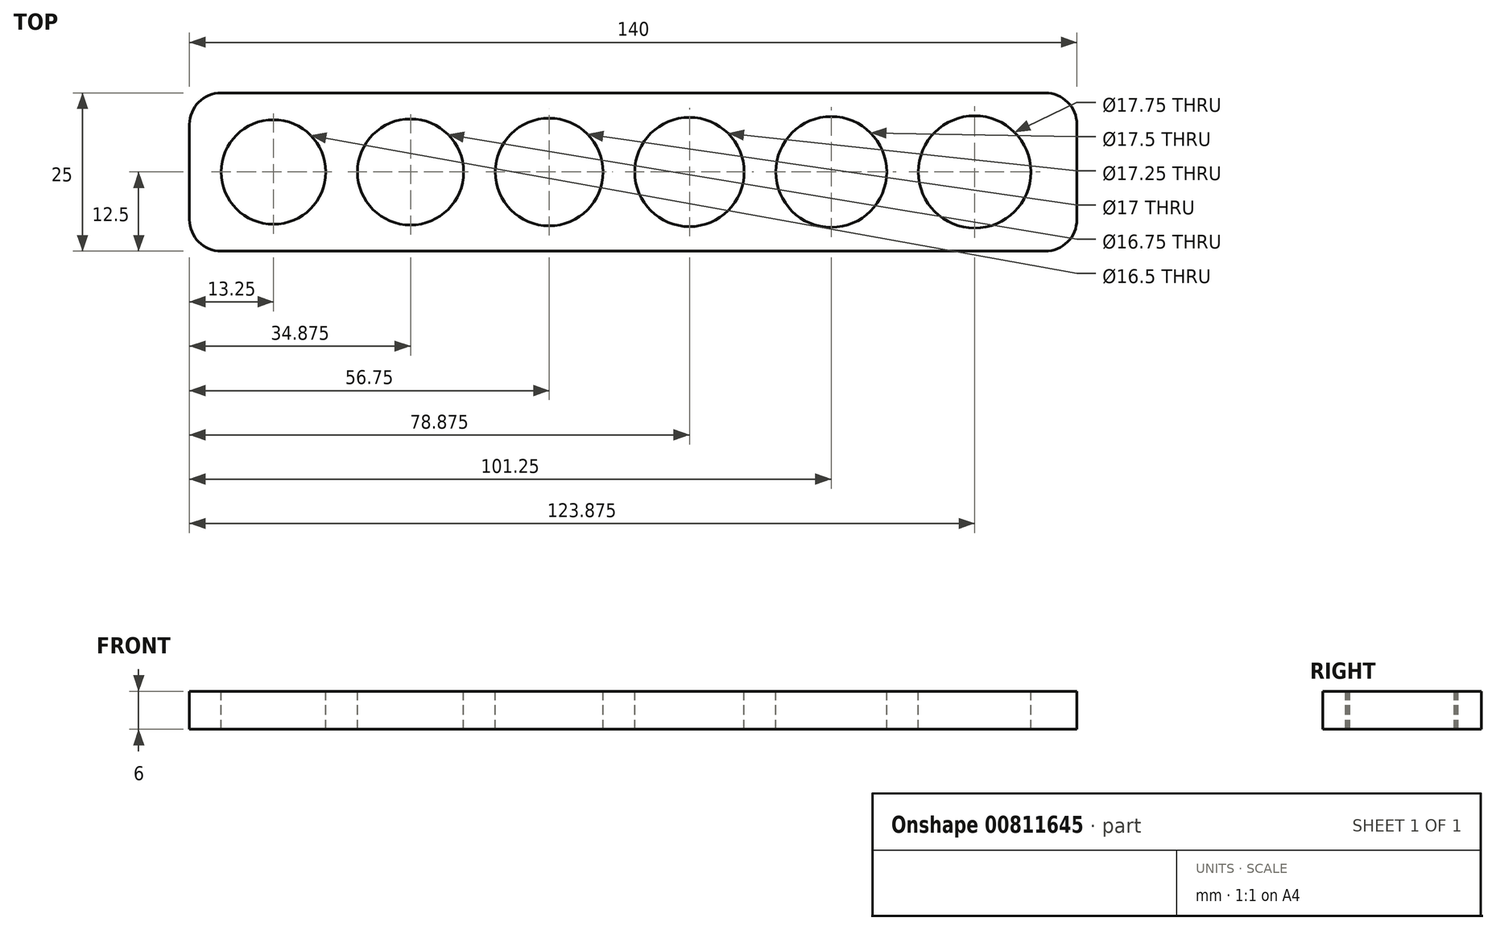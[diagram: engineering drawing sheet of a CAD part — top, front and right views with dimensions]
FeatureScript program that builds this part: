
annotation { "Feature Type Name" : "Feature", "Feature Type Description" : "" }
export const myFeature = defineFeature(function(context is Context, id is Id, definition is map)
    precondition{}
    {
        {
            var Q0;
            Q0=qCreatedBy(makeId("Top.planeOp"),FACE);
            var sketch = newSketch(context, id + "F0", { "sketchPlane" : qUnion([Q0])});
            skLineSegment(sketch, "E0.bottom", {"start": v(-65, 12.5) * mm, "end": v(65, 12.5) * mm});
            skLineSegment(sketch, "E0.top", {"start": v(-65, -12.5) * mm, "end": v(65, -12.5) * mm});
            skLineSegment(sketch, "E0.left", {"start": v(-70, 7.5) * mm, "end": v(-70, -7.5) * mm});
            skLineSegment(sketch, "E0.right", {"start": v(70, 7.5) * mm, "end": v(70, -7.5) * mm});
            skPoint(sketch, "E1.visualSharp", {"position": v(-70, 12.5) * mm});
            skArc(sketch, "E1.filletArc", {"start": v(-65, 12.5) * mm, "mid": v(-68.54, 11.04) * mm, "end": v(-70, 7.5) * mm});
            skPoint(sketch, "E2.visualSharp", {"position": v(70, 12.5) * mm});
            skArc(sketch, "E2.filletArc", {"start": v(70, 7.5) * mm, "mid": v(68.54, 11.04) * mm, "end": v(65, 12.5) * mm});
            skPoint(sketch, "E3.visualSharp", {"position": v(70, -12.5) * mm});
            skArc(sketch, "E3.filletArc", {"start": v(65, -12.5) * mm, "mid": v(68.54, -11.04) * mm, "end": v(70, -7.5) * mm});
            skPoint(sketch, "E4.visualSharp", {"position": v(-70, -12.5) * mm});
            skArc(sketch, "E4.filletArc", {"start": v(-70, -7.5) * mm, "mid": v(-68.54, -11.04) * mm, "end": v(-65, -12.5) * mm});
            skSolve(sketch);
        }
        {
            var Q0;
            Q0=makeQuery(id+"F0.imprint","IMPRINT",FACE,{"disambiguationData":[TD([[makeQuery(id+"F0.imprint","IMPRINT",EDGE,{"derivedFrom":sQuery(id+"F0.wireOp",EDGE,"E0.bottom")}),-1.0]])]});
            extrude(context, id + "F1", {"entities" : qUnion([Q0]), "depth" : 6 * mm, "offsetDistance" : 25 * mm});
        }
        {
            var Q0;
            Q0=makeQuery(id+"F1.opExtrude","CAP_FACE",FACE,{"disambiguationData":[OSD([sQuery(id+"F0.wireOp",EDGE,"E0.bottom"),sQuery(id+"F0.wireOp",EDGE,"E0.top"),sQuery(id+"F0.wireOp",EDGE,"E0.left"),sQuery(id+"F0.wireOp",EDGE,"E0.right")])],"isStart":false});
            var sketch = newSketch(context, id + "F2", { "sketchPlane" : qUnion([Q0])});
            skCircle(sketch, "E5", {"center": v(-56.75, 0) * mm, "radius": 8.25 * mm});
            skCircle(sketch, "E6", {"center": v(-35.12, 0) * mm, "radius": 8.38 * mm});
            skCircle(sketch, "E7", {"center": v(-13.25, 0) * mm, "radius": 8.5 * mm});
            skCircle(sketch, "E8", {"center": v(8.88, 0) * mm, "radius": 8.62 * mm});
            skCircle(sketch, "E9", {"center": v(31.25, 0) * mm, "radius": 8.75 * mm});
            skCircle(sketch, "E10", {"center": v(53.88, 0) * mm, "radius": 8.88 * mm});
            skSolve(sketch);
        }
        {
            var Q0;
            Q0 = qSketchRegion(id + "F2", true);
            extrude(context, id + "F3", {"entities" : qUnion([Q0]), "operationType" : NewBodyOperationType.REMOVE, "endBound" : BoundingType.THROUGH_ALL, "oppositeDirection" : true, "depth" : 25 * mm, "offsetDistance" : 25 * mm});
        }
    });
